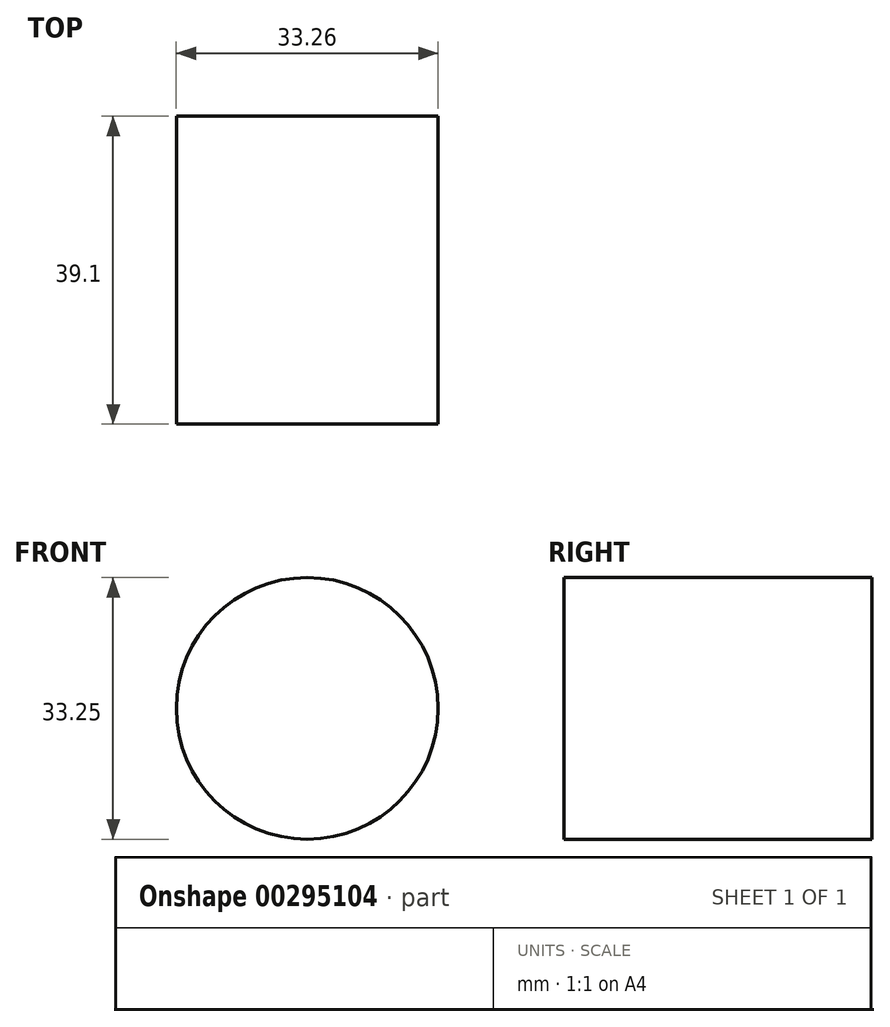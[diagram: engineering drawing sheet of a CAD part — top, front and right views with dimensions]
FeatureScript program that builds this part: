
annotation { "Feature Type Name" : "Feature", "Feature Type Description" : "" }
export const myFeature = defineFeature(function(context is Context, id is Id, definition is map)
    precondition{}
    {
        {
            var Q0;
            Q0=qCreatedBy(makeId("Front.planeOp"),FACE);
            var sketch = newSketch(context, id + "F0", { "sketchPlane" : qUnion([Q0])});
            skCircle(sketch, "E0", {"center": v(-44.6, 34.52) * mm, "radius": 16.63 * mm});
            skSolve(sketch);
        }
        {
            var Q0;
            Q0 = qSketchRegion(id + "F0", true);
            extrude(context, id + "F1", {"entities" : qUnion([Q0]), "depth" : 39.1 * mm});
        }
    });
